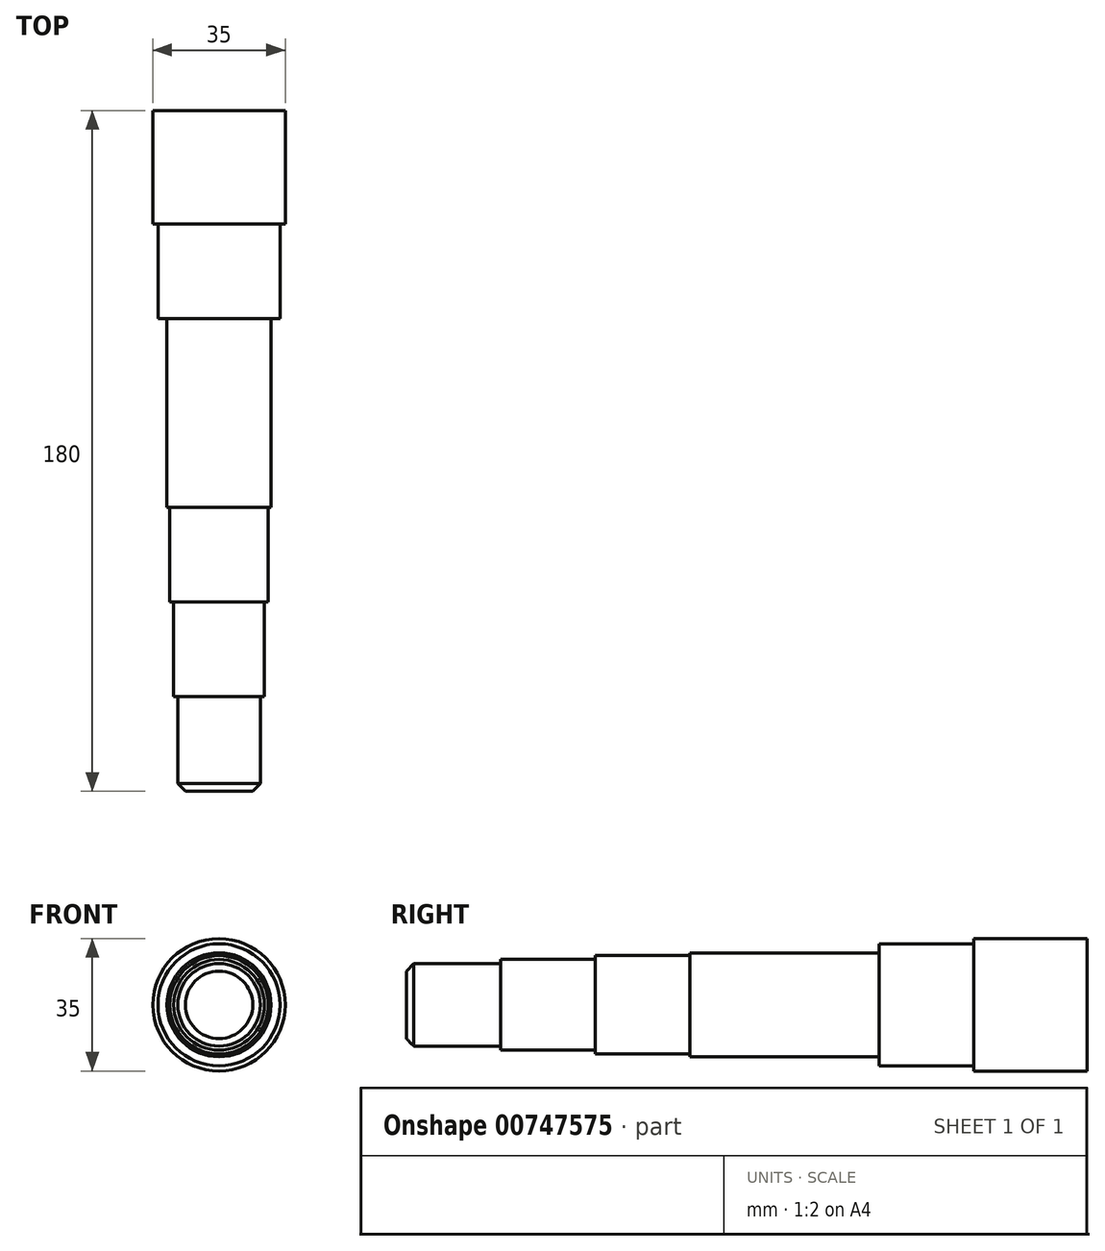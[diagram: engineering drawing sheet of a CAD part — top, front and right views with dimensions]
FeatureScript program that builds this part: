
annotation { "Feature Type Name" : "Feature", "Feature Type Description" : "" }
export const myFeature = defineFeature(function(context is Context, id is Id, definition is map)
    precondition{}
    {
        {
            var Q0;
            Q0=qCreatedBy(makeId("Front.planeOp"),FACE);
            var sketch = newSketch(context, id + "F0", { "sketchPlane" : qUnion([Q0])});
            skCircle(sketch, "E0", {"center": v(0, 0) * mm, "radius": 17.5 * mm});
            skSolve(sketch);
        }
        {
            var Q0;
            Q0=makeQuery(id+"F0.imprint","IMPRINT",FACE,{"disambiguationData":[TD([[makeQuery(id+"F0.imprint","IMPRINT",EDGE,{"derivedFrom":sQuery(id+"F0.wireOp",EDGE,"E0")}),1.0]])]});
            extrude(context, id + "F1", {"entities" : qUnion([Q0]), "depth" : 30 * mm, "offsetDistance" : 25 * mm});
        }
        {
            var Q0;
            Q0=makeQuery(id+"F1.opExtrude","CAP_FACE",FACE,{"disambiguationData":[OSD([sQuery(id+"F0.wireOp",EDGE,"E0")])],"isStart":false});
            var sketch = newSketch(context, id + "F2", { "sketchPlane" : qUnion([Q0])});
            skCircle(sketch, "E1", {"center": v(0, 0) * mm, "radius": 16.12 * mm});
            skSolve(sketch);
        }
        {
            var Q0;
            Q0 = qSketchRegion(id + "F2", true);
            extrude(context, id + "F3", {"entities" : qUnion([Q0]), "operationType" : NewBodyOperationType.ADD, "depth" : 25 * mm, "offsetDistance" : 25 * mm});
        }
        {
            var Q0;
            Q0=makeQuery(id+"F3.opExtrude","CAP_FACE",FACE,{"disambiguationData":[OSD([sQuery(id+"F2.wireOp",EDGE,"E1")])],"isStart":false});
            var sketch = newSketch(context, id + "F4", { "sketchPlane" : qUnion([Q0])});
            skCircle(sketch, "E2", {"center": v(0, 0) * mm, "radius": 13.75 * mm});
            skSolve(sketch);
        }
        {
            var Q0;
            Q0 = qSketchRegion(id + "F4", true);
            extrude(context, id + "F5", {"entities" : qUnion([Q0]), "operationType" : NewBodyOperationType.ADD, "depth" : 50 * mm, "offsetDistance" : 25 * mm});
        }
        {
            var Q0;
            Q0=makeQuery(id+"F5.opExtrude","CAP_FACE",FACE,{"disambiguationData":[OSD([sQuery(id+"F4.wireOp",EDGE,"E2")])],"isStart":false});
            var sketch = newSketch(context, id + "F6", { "sketchPlane" : qUnion([Q0])});
            skCircle(sketch, "E3", {"center": v(0, 0) * mm, "radius": 13 * mm});
            skSolve(sketch);
        }
        {
            var Q0;
            Q0 = qSketchRegion(id + "F6", true);
            extrude(context, id + "F7", {"entities" : qUnion([Q0]), "operationType" : NewBodyOperationType.ADD, "depth" : 25 * mm, "offsetDistance" : 25 * mm});
        }
        {
            var Q0;
            Q0=makeQuery(id+"F7.opExtrude","CAP_FACE",FACE,{"disambiguationData":[OSD([sQuery(id+"F6.wireOp",EDGE,"E3")])],"isStart":false});
            var sketch = newSketch(context, id + "F8", { "sketchPlane" : qUnion([Q0])});
            skCircle(sketch, "E4", {"center": v(0, 0) * mm, "radius": 11.98 * mm});
            skSolve(sketch);
        }
        {
            var Q0;
            Q0 = qSketchRegion(id + "F8", true);
            extrude(context, id + "F9", {"entities" : qUnion([Q0]), "operationType" : NewBodyOperationType.ADD, "depth" : 25 * mm, "offsetDistance" : 25 * mm});
        }
        {
            var Q0;
            Q0=makeQuery(id+"F9.opExtrude","CAP_FACE",FACE,{"disambiguationData":[OSD([sQuery(id+"F8.wireOp",EDGE,"E4")])],"isStart":false});
            var sketch = newSketch(context, id + "F10", { "sketchPlane" : qUnion([Q0])});
            skCircle(sketch, "E5", {"center": v(0, 0) * mm, "radius": 10.91 * mm});
            skSolve(sketch);
        }
        {
            var Q0;
            Q0 = qSketchRegion(id + "F10", true);
            extrude(context, id + "F11", {"entities" : qUnion([Q0]), "operationType" : NewBodyOperationType.ADD, "depth" : 25 * mm, "offsetDistance" : 25 * mm});
        }
        {
            var Q0;
            Q0=makeQuery(id+"F11.opExtrude","CAP_EDGE",EDGE,{"disambiguationData":[OSD([sQuery(id+"F10.wireOp",EDGE,"E5")])],"isStart":false});
            chamfer(context, id + "F12", {"entities" : qUnion([Q0]), "width" : 2 * mm, "tangentPropagation" : true});
        }
    });
